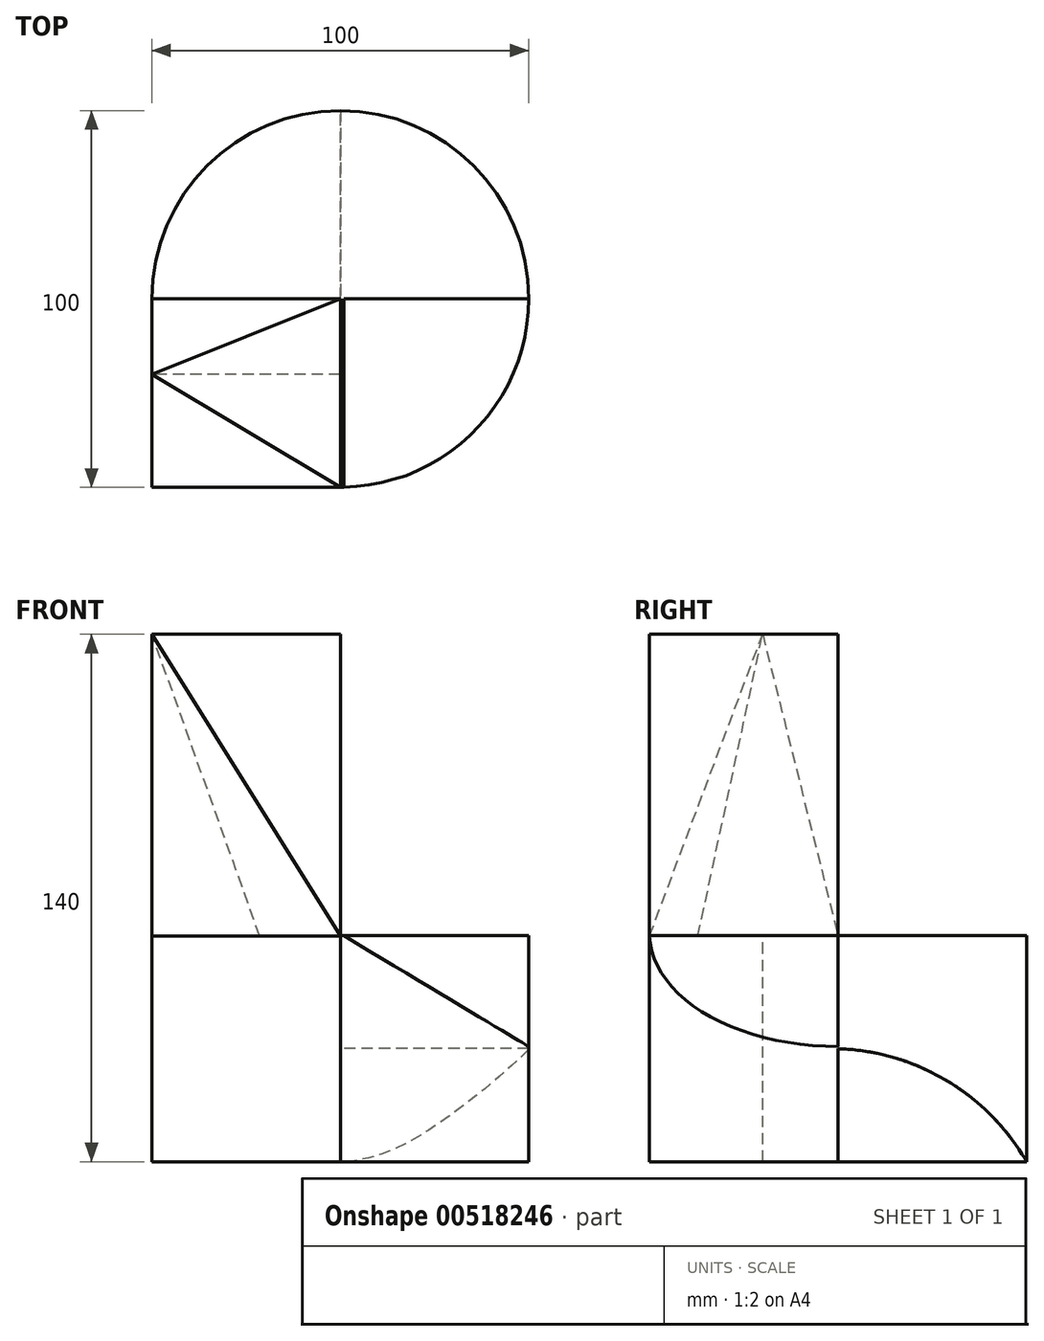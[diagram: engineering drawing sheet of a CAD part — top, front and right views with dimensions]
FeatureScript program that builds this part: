
annotation { "Feature Type Name" : "Feature", "Feature Type Description" : "" }
export const myFeature = defineFeature(function(context is Context, id is Id, definition is map)
    precondition{}
    {
        {
            var Q0;
            Q0=qCreatedBy(makeId("Top.planeOp"),FACE);
            var sketch = newSketch(context, id + "F0", { "sketchPlane" : qUnion([Q0])});
            skCircle(sketch, "E0", {"center": v(0, 0) * mm, "radius": 50 * mm});
            skSolve(sketch);
        }
        {
            var Q0;
            Q0 = qSketchRegion(id + "F0", true);
            extrude(context, id + "F1", {"entities" : qUnion([Q0]), "depth" : 60 * mm, "offsetDistance" : 25 * mm});
        }
        {
            var Q0;
            Q0=makeQuery(id+"F1.opExtrude","CAP_FACE",FACE,{"disambiguationData":[OSD([sQuery(id+"F0.wireOp",EDGE,"E0")])],"isStart":false});
            var sketch = newSketch(context, id + "F2", { "sketchPlane" : qUnion([Q0])});
            skLineSegment(sketch, "E1", {"start": v(0, 0) * mm, "end": v(0, -50) * mm});
            skLineSegment(sketch, "E2", {"start": v(0, 0) * mm, "end": v(-50, 0) * mm});
            skSolve(sketch);
        }
        {
            var Q0;
            {var subQ0=sQuery(id+"F2.wireOp",EDGE,"E1");Q0=makeQuery(id+"F2.imprint","IMPRINT",FACE,{"disambiguationData":[TD([[makeQuery(id+"F2.imprint","IMPRINT",EDGE,{"derivedFrom":subQ0}),-1.0]])]});}
            extrude(context, id + "F3", {"entities" : qUnion([Q0]), "operationType" : NewBodyOperationType.REMOVE, "endBound" : BoundingType.THROUGH_ALL, "oppositeDirection" : true, "depth" : 25 * mm, "offsetDistance" : 25 * mm});
        }
        {
            var Q0;
            Q0=qCreatedBy(makeId("Top.planeOp"),FACE);
            var sketch = newSketch(context, id + "F4", { "sketchPlane" : qUnion([Q0])});
            skLineSegment(sketch, "E3.bottom", {"start": v(0, 0) * mm, "end": v(-50, 0) * mm});
            skLineSegment(sketch, "E3.top", {"start": v(0, -50) * mm, "end": v(-50, -50) * mm});
            skLineSegment(sketch, "E3.left", {"start": v(0, 0) * mm, "end": v(0, -50) * mm});
            skLineSegment(sketch, "E3.right", {"start": v(-50, 0) * mm, "end": v(-50, -50) * mm});
            skSolve(sketch);
        }
        {
            var Q0;
            Q0=makeQuery(id+"F4.imprint","IMPRINT",FACE,{"disambiguationData":[TD([[makeQuery(id+"F4.imprint","IMPRINT",EDGE,{"derivedFrom":sQuery(id+"F4.wireOp",EDGE,"E3.bottom")}),1.0]])]});
            extrude(context, id + "F5", {"entities" : qUnion([Q0]), "operationType" : NewBodyOperationType.ADD, "depth" : 140 * mm, "offsetDistance" : 25 * mm});
        }
        {
            var Q0;
            Q0=makeQuery(id+"F5.opExtrude","SWEPT_FACE",FACE,{"disambiguationData":[OSD([sQuery(id+"F4.wireOp",EDGE,"E3.right")])]});
            var sketch = newSketch(context, id + "F6", { "sketchPlane" : qUnion([Q0])});
            skLineSegment(sketch, "E4.bottom", {"start": v(50, 0) * mm, "end": v(20, 0) * mm});
            skLineSegment(sketch, "E4.top", {"start": v(50, 59.9) * mm, "end": v(20, 59.9) * mm});
            skLineSegment(sketch, "E4.left", {"start": v(50, 0) * mm, "end": v(50, 59.9) * mm});
            skLineSegment(sketch, "E4.right", {"start": v(20, 0) * mm, "end": v(20, 59.9) * mm});
            skSolve(sketch);
        }
        {
            var Q0;
            Q0=makeQuery(id+"F6.imprint","IMPRINT",FACE,{"disambiguationData":[TD([[makeQuery(id+"F6.imprint","IMPRINT",EDGE,{"derivedFrom":sQuery(id+"F6.wireOp",EDGE,"E4.bottom")}),1.0]])]});
            extrude(context, id + "F7", {"entities" : qUnion([Q0]), "operationType" : NewBodyOperationType.REMOVE, "oppositeDirection" : true, "depth" : 50 * mm, "offsetDistance" : 25 * mm});
        }
        {
            var Q0;
            Q0=makeQuery(id+"F5.opExtrude","CAP_FACE",FACE,{"disambiguationData":[OSD([sQuery(id+"F4.wireOp",EDGE,"E3.bottom"),sQuery(id+"F4.wireOp",EDGE,"E3.top"),sQuery(id+"F4.wireOp",EDGE,"E3.left"),sQuery(id+"F4.wireOp",EDGE,"E3.right")])],"isStart":false});
            var sketch = newSketch(context, id + "F8", { "sketchPlane" : qUnion([Q0])});
            skLineSegment(sketch, "E5", {"start": v(-50, -20) * mm, "end": v(0, -50) * mm});
            skSolve(sketch);
        }
        {
            var Q1;
            Q1=makeQuery(id+"F5.opExtrude","SWEPT_FACE",FACE,{"disambiguationData":[OSD([sQuery(id+"F4.wireOp",EDGE,"E3.top")])]});
            var Q2;
            Q2=sQuery(id+"F8.wireOp",VERTEX,"E5.start");
            loft(context, id + "F9", {"operationType" : NewBodyOperationType.REMOVE, "sheetProfilesArray" : [{ "sheetProfileEntities" : qUnion([Q1]) }, { "sheetProfileEntities" : qUnion([Q2]) }]});
        }
        {
            var Q0;
            Q0=makeQuery(id+"F5.opExtrude","CAP_FACE",FACE,{"disambiguationData":[OSD([sQuery(id+"F4.wireOp",EDGE,"E3.bottom"),sQuery(id+"F4.wireOp",EDGE,"E3.top"),sQuery(id+"F4.wireOp",EDGE,"E3.left"),sQuery(id+"F4.wireOp",EDGE,"E3.right")])],"isStart":false});
            var sketch = newSketch(context, id + "F10", { "sketchPlane" : qUnion([Q0])});
            skLineSegment(sketch, "E6", {"start": v(-50, -20) * mm, "end": v(0, 0) * mm});
            skSolve(sketch);
        }
        {
            var Q1;
            Q1=makeQuery(id+"F10.imprint","IMPRINT",FACE,{"disambiguationData":[TD([[makeQuery(id+"F10.imprint","IMPRINT",EDGE,{"derivedFrom":sQuery(id+"F10.wireOp",EDGE,"E6")}),1.0]])]});
            var Q2;
            Q2=makeQuery(id+"F3.boolean.opBoolean","COPY",VERTEX,{"derivedFrom":makeQuery(id+"F3.opExtrude","CAP_VERTEX",VERTEX,{"disambiguationData":[OSD([sQuery(id+"F2.wireOp",EDGE,"E1"),sQuery(id+"F2.wireOp",EDGE,"E2")])],"isStart":true})});
            loft(context, id + "F11", {"operationType" : NewBodyOperationType.REMOVE, "sheetProfilesArray" : [{ "sheetProfileEntities" : qUnion([Q1]) }, { "sheetProfileEntities" : qUnion([Q2]) }]});
        }
        {
            var Q0;
            Q0=qCreatedBy(makeId("Front.planeOp"),FACE);
            var sketch = newSketch(context, id + "F12", { "sketchPlane" : qUnion([Q0])});
            skLineSegment(sketch, "E7", {"start": v(0, 60.52) * mm, "end": v(50, 60.52) * mm});
            skLineSegment(sketch, "E8", {"start": v(50, 60.52) * mm, "end": v(50, 30.52) * mm});
            skLineSegment(sketch, "E9", {"start": v(50, 30.52) * mm, "end": v(0, 60.52) * mm});
            skSolve(sketch);
        }
        {
            var Q0;
            Q0 = qSketchRegion(id + "F12", true);
            extrude(context, id + "F13", {"entities" : qUnion([Q0]), "operationType" : NewBodyOperationType.REMOVE, "endBound" : BoundingType.THROUGH_ALL, "depth" : 25 * mm, "offsetDistance" : 25 * mm});
        }
        {
            var Q0;
            Q0=qCreatedBy(makeId("Right.planeOp"),FACE);
            var sketch = newSketch(context, id + "F14", { "sketchPlane" : qUnion([Q0])});
            skLineSegment(sketch, "E10", {"start": v(0, 0) * mm, "end": v(0, 29.99) * mm});
            skArc(sketch, "E11", {"start": v(50, 0) * mm, "mid": v(28.89, 21.48) * mm, "end": v(0, 29.99) * mm});
            skLineSegment(sketch, "E12", {"start": v(0, 0) * mm, "end": v(50, 0) * mm});
            skSolve(sketch);
        }
        {
            var Q0;
            Q0 = qSketchRegion(id + "F14", true);
            extrude(context, id + "F15", {"entities" : qUnion([Q0]), "operationType" : NewBodyOperationType.REMOVE, "endBound" : BoundingType.UP_TO_NEXT, "depth" : 25 * mm, "offsetDistance" : 25 * mm});
        }
    });
